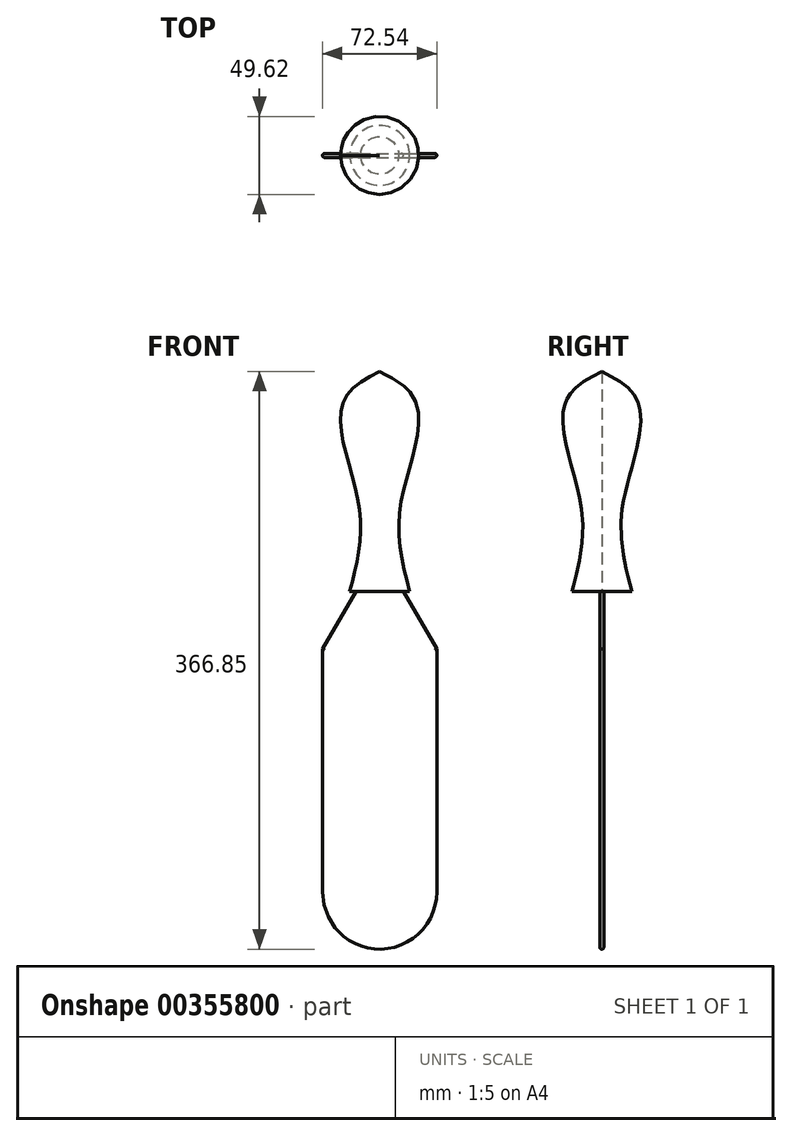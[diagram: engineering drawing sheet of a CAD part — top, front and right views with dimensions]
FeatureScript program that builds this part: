
annotation { "Feature Type Name" : "Feature", "Feature Type Description" : "" }
export const myFeature = defineFeature(function(context is Context, id is Id, definition is map)
    precondition{}
    {
        {
            var Q0;
            Q0=qCreatedBy(makeId("Top.planeOp"),FACE);
            var sketch = newSketch(context, id + "F0", { "sketchPlane" : qUnion([Q0])});
            skCircle(sketch, "E0", {"center": v(0, 0) * mm, "radius": 12.7 * mm});
            skSolve(sketch);
        }
        {
            var Q0;
            Q0=qCreatedBy(makeId("Top.planeOp"),FACE);
            cPlane(context, id + "F1", {"entities" : qUnion([Q0]), "cplaneType" : CPlaneType.OFFSET, "offset" : 76.2 * mm, "width" : 152.4 * mm, "height" : 152.4 * mm});
        }
        {
            var Q0;
            Q0=qCreatedBy(makeId("Top.planeOp"),FACE);
            cPlane(context, id + "F2", {"entities" : qUnion([Q0]), "cplaneType" : CPlaneType.OFFSET, "offset" : 50.8 * mm, "oppositeDirection" : true, "width" : 152.4 * mm, "height" : 152.4 * mm});
        }
        {
            var Q0;
            Q0=qCreatedBy(id+"F1.planeOp",FACE);
            var sketch = newSketch(context, id + "F3", { "sketchPlane" : qUnion([Q0])});
            skCircle(sketch, "E1", {"center": v(0, 0) * mm, "radius": 19.05 * mm});
            skSolve(sketch);
        }
        {
            var Q0;
            Q0=qCreatedBy(id+"F2.planeOp",FACE);
            var sketch = newSketch(context, id + "F4", { "sketchPlane" : qUnion([Q0])});
            skCircle(sketch, "E2", {"center": v(0, 0) * mm, "radius": 19.05 * mm});
            skSolve(sketch);
        }
        {
            var Q0;
            Q0=qCreatedBy(id+"F1.planeOp",FACE);
            cPlane(context, id + "F5", {"entities" : qUnion([Q0]), "cplaneType" : CPlaneType.OFFSET, "offset" : 12.7 * mm, "width" : 152.4 * mm, "height" : 152.4 * mm});
        }
        {
            var Q0;
            Q0=qCreatedBy(id+"F5.planeOp",FACE);
            var sketch = newSketch(context, id + "F6", { "sketchPlane" : qUnion([Q0])});
            skCircle(sketch, "E3", {"center": v(0, 0) * mm, "radius": 1.27 * mm});
            skSolve(sketch);
        }
        {
            var Q0;
            Q0=sQuery(id+"F6.wireOp",VERTEX,"E3.center");
            var Q1;
            Q1=makeQuery(id+"F3.imprint","IMPRINT",FACE,{"disambiguationData":[TD([[makeQuery(id+"F3.imprint","IMPRINT",EDGE,{"derivedFrom":sQuery(id+"F3.wireOp",EDGE,"E1")}),1.0]])]});
            var Q2;
            Q2=makeQuery(id+"F0.imprint","IMPRINT",FACE,{"disambiguationData":[TD([[makeQuery(id+"F0.imprint","IMPRINT",EDGE,{"derivedFrom":sQuery(id+"F0.wireOp",EDGE,"E0")}),1.0]])]});
            var Q3;
            Q3=makeQuery(id+"F4.imprint","IMPRINT",FACE,{"disambiguationData":[TD([[makeQuery(id+"F4.imprint","IMPRINT",EDGE,{"derivedFrom":sQuery(id+"F4.wireOp",EDGE,"E2")}),1.0]])]});
            loft(context, id + "F7", {"sheetProfilesArray" : [{ "sheetProfileEntities" : qUnion([Q0]) }, { "sheetProfileEntities" : qUnion([Q1]) }, { "sheetProfileEntities" : qUnion([Q2]) }, { "sheetProfileEntities" : qUnion([Q3]) }]});
        }
        {
            var Q0;
            Q0=qCreatedBy(makeId("Front.planeOp"),FACE);
            var sketch = newSketch(context, id + "F8", { "sketchPlane" : qUnion([Q0])});
            skLineSegment(sketch, "E4", {"start": v(0, -47.68) * mm, "end": v(13.27, -47.68) * mm});
            skLineSegment(sketch, "E5", {"start": v(13.27, -47.68) * mm, "end": v(36.26, -87.2) * mm});
            skLineSegment(sketch, "E6", {"start": v(0, -47.68) * mm, "end": v(-13.14, -47.68) * mm});
            skPoint(sketch, "E6.endSnap0", {"position": v(6.64, -47.68) * mm});
            skLineSegment(sketch, "E7", {"start": v(-13.14, -47.68) * mm, "end": v(-36.28, -87.2) * mm});
            skLineSegment(sketch, "E8", {"start": v(-36.28, -87.2) * mm, "end": v(36.26, -87.2) * mm});
            skLineSegment(sketch, "E9", {"start": v(36.26, -87.2) * mm, "end": v(36.26, -241.68) * mm});
            skLineSegment(sketch, "E10", {"start": v(36.26, -241.68) * mm, "end": v(-36.28, -241.68) * mm});
            skLineSegment(sketch, "E11", {"start": v(-36.28, -241.68) * mm, "end": v(-36.28, -87.2) * mm});
            skArc(sketch, "E12", {"start": v(-36.28, -241.68) * mm, "mid": v(-0.01, -277.95) * mm, "end": v(36.26, -241.68) * mm});
            skSolve(sketch);
        }
        {
            var Q0;
            Q0 = qSketchRegion(id + "F8", true);
            extrude(context, id + "F9", {"entities" : qUnion([Q0]), "operationType" : NewBodyOperationType.ADD, "endBound" : BoundingType.SYMMETRIC, "oppositeDirection" : true, "depth" : 2.54 * mm});
        }
        {
            var Q0;
            Q0=makeQuery(id+"F9.opExtrude","CAP_EDGE",EDGE,{"disambiguationData":[OSD([sQuery(id+"F8.wireOp",EDGE,"E11")])],"isStart":true});
            var Q1;
            Q1=makeQuery(id+"F9.opExtrude","CAP_EDGE",EDGE,{"disambiguationData":[OSD([sQuery(id+"F8.wireOp",EDGE,"E11")])],"isStart":false});
            var Q2;
            Q2=makeQuery(id+"F9.opExtrude","CAP_EDGE",EDGE,{"disambiguationData":[OSD([sQuery(id+"F8.wireOp",EDGE,"E9")])],"isStart":true});
            var Q3;
            Q3=makeQuery(id+"F9.opExtrude","CAP_EDGE",EDGE,{"disambiguationData":[OSD([sQuery(id+"F8.wireOp",EDGE,"E9")])],"isStart":false});
            var Q4;
            Q4=makeQuery(id+"F9.opExtrude","CAP_EDGE",EDGE,{"disambiguationData":[OSD([sQuery(id+"F8.wireOp",EDGE,"E5")])],"isStart":true});
            var Q5;
            Q5=makeQuery(id+"F9.opExtrude","CAP_EDGE",EDGE,{"disambiguationData":[OSD([sQuery(id+"F8.wireOp",EDGE,"E5")])],"isStart":false});
            var Q6;
            Q6=makeQuery(id+"F9.opExtrude","CAP_EDGE",EDGE,{"disambiguationData":[OSD([sQuery(id+"F8.wireOp",EDGE,"E7")])],"isStart":false});
            var Q7;
            Q7=makeQuery(id+"F9.opExtrude","CAP_EDGE",EDGE,{"disambiguationData":[OSD([sQuery(id+"F8.wireOp",EDGE,"E7")])],"isStart":true});
            var Q8;
            Q8=makeQuery(id+"F9.opExtrude","CAP_EDGE",EDGE,{"disambiguationData":[OSD([sQuery(id+"F8.wireOp",EDGE,"E12")])],"isStart":true});
            var Q9;
            Q9=makeQuery(id+"F9.opExtrude","CAP_EDGE",EDGE,{"disambiguationData":[OSD([sQuery(id+"F8.wireOp",EDGE,"E12")])],"isStart":false});
            fillet(context, id + "F10", {"entities" : qUnion([Q0, Q1, Q2, Q3, Q4, Q5, Q6, Q7, Q8, Q9]), "radius" : 1.27 * mm, "tangentPropagation" : true, "allowEdgeOverflow" : false});
        }
        {
            var Q0;
            Q0=qCreatedBy(makeId("Front.planeOp"),FACE);
            var sketch = newSketch(context, id + "F11", { "sketchPlane" : qUnion([Q0])});
            skCircle(sketch, "E13", {"center": v(0, -34.2) * mm, "radius": 5.08 * mm});
            skSolve(sketch);
        }
        {
            var Q0;
            Q0=sQuery(id+"F11.wireOp",EDGE,"E13");
            extrude(context, id + "F12", {"bodyType" : ToolBodyType.SURFACE, "surfaceEntities" : qUnion([Q0]), "oppositeDirection" : true, "depth" : 17.78 * mm});
        }
    });
